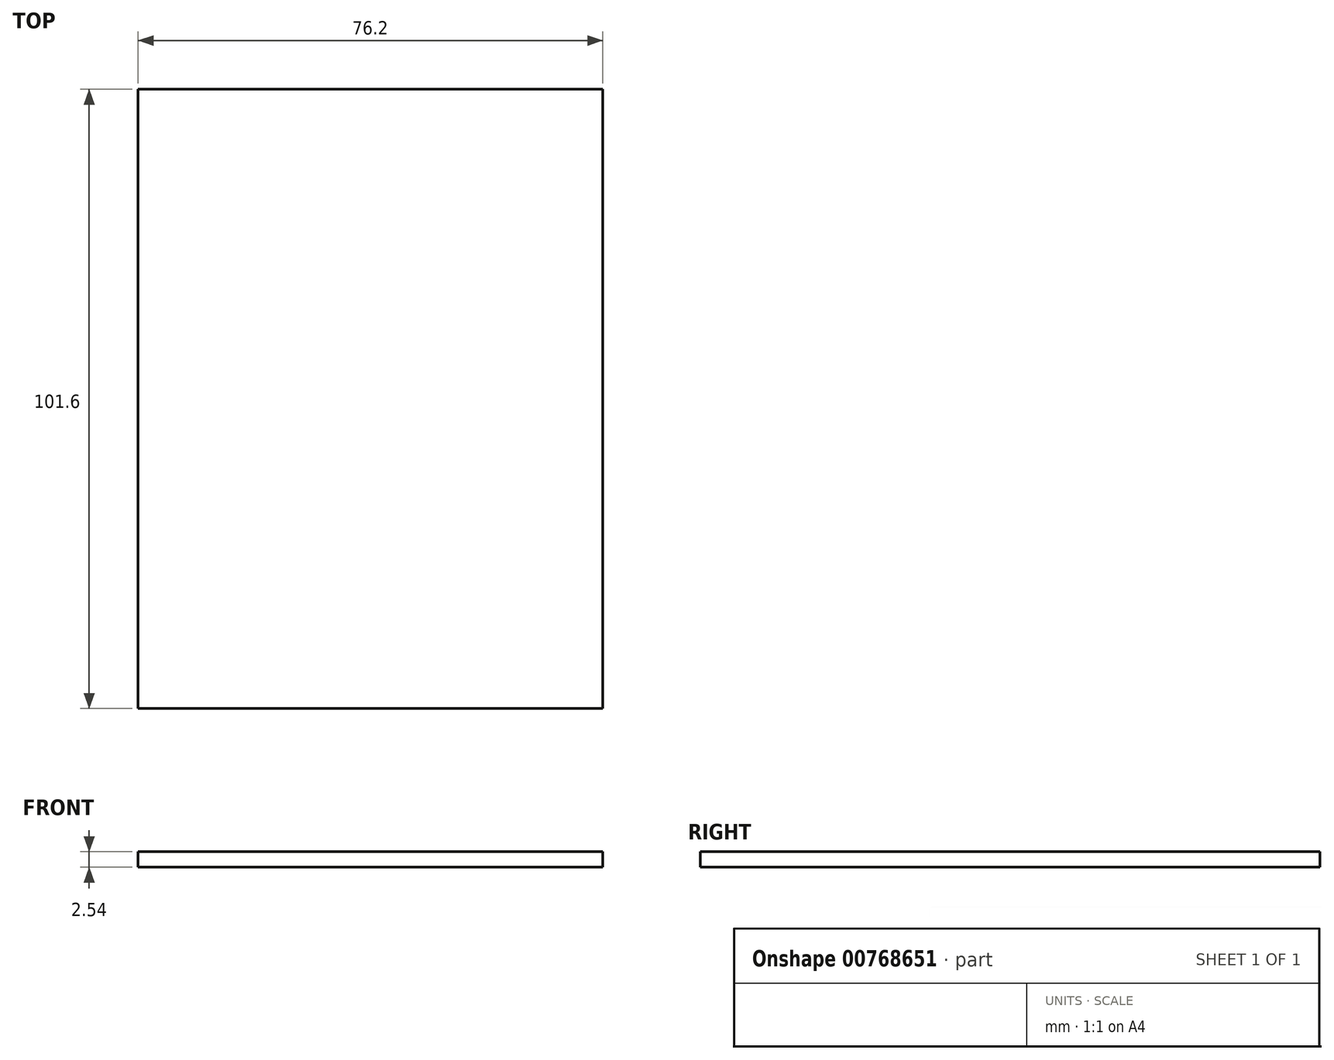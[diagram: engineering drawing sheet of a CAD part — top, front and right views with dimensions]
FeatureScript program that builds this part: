
annotation { "Feature Type Name" : "Feature", "Feature Type Description" : "" }
export const myFeature = defineFeature(function(context is Context, id is Id, definition is map)
    precondition{}
    {
        {
            var Q0;
            Q0=qCreatedBy(makeId("Top.planeOp"),FACE);
            var sketch = newSketch(context, id + "F0", { "sketchPlane" : qUnion([Q0])});
            skLineSegment(sketch, "E0", {"start": v(0, 0) * mm, "end": v(0, -101.6) * mm});
            skLineSegment(sketch, "E1", {"start": v(0, 0) * mm, "end": v(76.2, 0) * mm});
            skLineSegment(sketch, "E2", {"start": v(76.2, 0) * mm, "end": v(76.2, -101.6) * mm});
            skLineSegment(sketch, "E3", {"start": v(76.2, -101.6) * mm, "end": v(0, -101.6) * mm});
            skSolve(sketch);
        }
        {
            var Q0;
            Q0=makeQuery(id+"F0.imprint","IMPRINT",FACE,{"disambiguationData":[TD([[makeQuery(id+"F0.imprint","IMPRINT",EDGE,{"derivedFrom":sQuery(id+"F0.wireOp",EDGE,"E0")}),1.0]])]});
            extrude(context, id + "F1", {"entities" : qUnion([Q0]), "depth" : 2.54 * mm, "offsetDistance" : 25.4 * mm});
        }
    });
